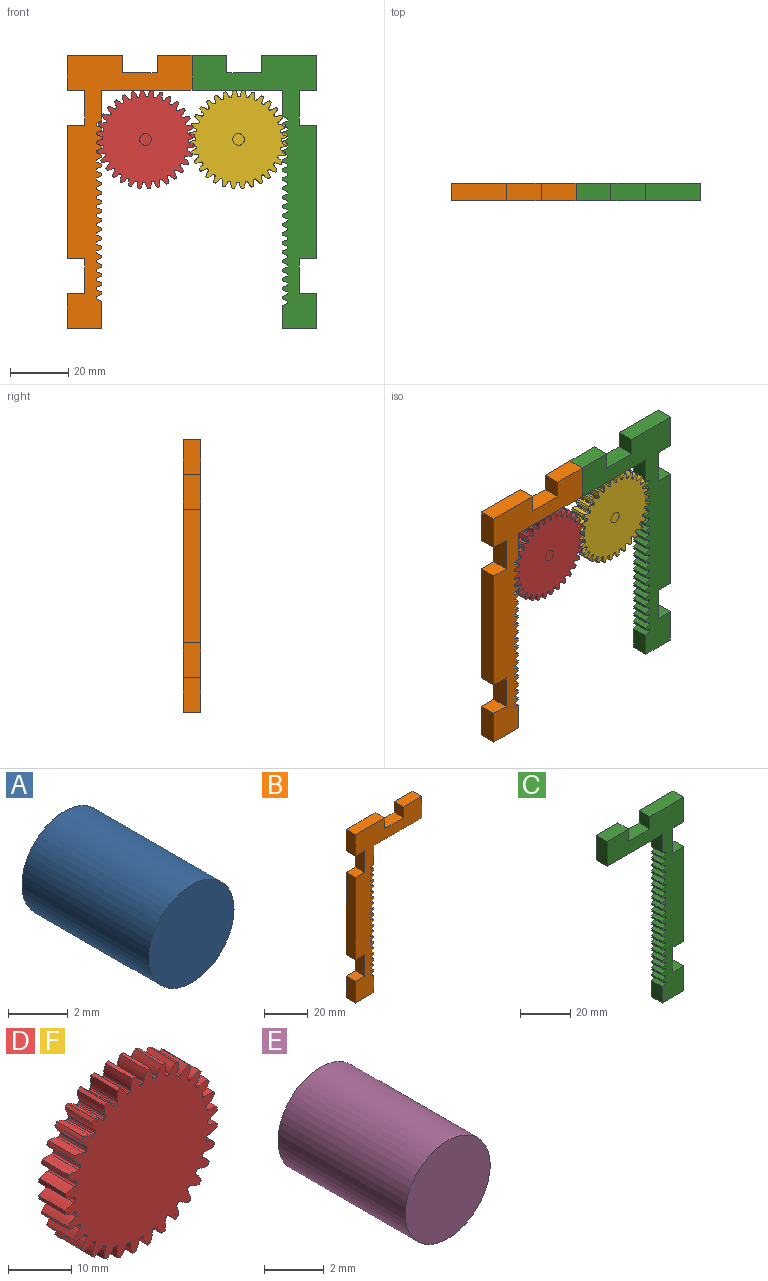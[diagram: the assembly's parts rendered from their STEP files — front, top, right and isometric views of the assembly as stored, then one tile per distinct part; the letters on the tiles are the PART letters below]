
ASSEMBLY  parts=6 mates=5
PART A: 3 faces, bbox 4x6x4 mm
  f0: cylinder r=2mm len=6mm, axis (0,1,0), area 75.4mm2, adj f1,f2
  f1: plane 4x4mm, normal (0,-1,0), area 12.6mm2, adj f0
  f2: plane 4x4mm, normal (0,1,0), area 12.6mm2, adj f0
PART B: 100 faces, bbox 43x6x94 mm
  f0: plane 6x0.84mm, normal (1,0,0), area 5.1mm2, adj f1,f97,f98,f99
  f1: plane 6x2mm, normal (0.34,0,0.94), area 12.8mm2, adj f0,f2,f98,f99
  f2: plane 6x0.84mm, normal (1,0,0), area 5.1mm2, adj f1,f3,f98,f99
  f3: plane 6x2mm, normal (0.34,0,-0.94), area 12.8mm2, adj f2,f4,f98,f99
  f4: plane 10.57x6mm, normal (1,0,0), area 63.4mm2, adj f3,f5,f98,f99
  f5: plane 31x6mm, normal (0,0,-1), area 186mm2, adj f4,f6,f98,f99
  f6: plane 12x6mm, normal (1,0,0), area 72mm2, adj f5,f7,f98,f99
  f7: plane 12x6mm, normal (0,0,1), area 72mm2, adj f6,f8,f98,f99
  f8: plane 6x6mm, normal (-1,0,0), area 36mm2, adj f7,f9,f98,f99
  f9: plane 12x6mm, normal (0,0,1), area 72mm2, adj f8,f10,f98,f99
  f10: plane 6x6mm, normal (1,0,0), area 36mm2, adj f9,f11,f98,f99
  f11: plane 19x6mm, normal (0,0,1), area 114mm2, adj f10,f12,f98,f99
  f12: plane 12x6mm, normal (-1,0,0), area 72mm2, adj f11,f13,f98,f99
  f13: plane 6x6mm, normal (0,0,-1), area 36mm2, adj f12,f14,f98,f99
  f14: plane 12x6mm, normal (-1,0,0), area 72mm2, adj f13,f15,f98,f99
  f15: plane 6x6mm, normal (0,0,1), area 36mm2, adj f14,f16,f98,f99
  f16: plane 46x6mm, normal (-1,0,0), area 276mm2, adj f15,f17,f98,f99
  f17: plane 6x6mm, normal (0,0,-1), area 36mm2, adj f16,f18,f98,f99
  f18: plane 12x6mm, normal (-1,0,0), area 72mm2, adj f17,f19,f98,f99
  f19: plane 6x6mm, normal (0,0,1), area 36mm2, adj f18,f20,f98,f99
  f20: plane 12x6mm, normal (-1,0,0), area 72mm2, adj f19,f21,f98,f99
  f21: plane 12x6mm, normal (0,0,-1), area 72mm2, adj f20,f22,f98,f99
  f22: plane 9.44x6mm, normal (1,0,0), area 56.7mm2, adj f21,f23,f98,f99
  f23: plane 6x2mm, normal (0.34,0,0.94), area 12.8mm2, adj f22,f24,f98,f99
  f24: plane 6x0.84mm, normal (1,0,0), area 5.1mm2, adj f23,f25,f98,f99
  f25: plane 6x2mm, normal (0.34,0,-0.94), area 12.8mm2, adj f24,f26,f98,f99
  f26: plane 6x0.84mm, normal (1,0,0), area 5.1mm2, adj f25,f27,f98,f99
  f27: plane 6x2mm, normal (0.34,0,0.94), area 12.8mm2, adj f26,f28,f98,f99
  f28: plane 6x0.84mm, normal (1,0,0), area 5.1mm2, adj f27,f29,f98,f99
  f29: plane 6x2mm, normal (0.34,0,-0.94), area 12.8mm2, adj f28,f30,f98,f99
  f30: plane 6x0.84mm, normal (1,0,0), area 5.1mm2, adj f29,f31,f98,f99
  f31: plane 6x2mm, normal (0.34,0,0.94), area 12.8mm2, adj f30,f32,f98,f99
  f32: plane 6x0.84mm, normal (1,0,0), area 5.1mm2, adj f31,f33,f98,f99
  f33: plane 6x2mm, normal (0.34,0,-0.94), area 12.8mm2, adj f32,f34,f98,f99
  f34: plane 6x0.84mm, normal (1,0,0), area 5.1mm2, adj f33,f35,f98,f99
  f35: plane 6x2mm, normal (0.34,0,0.94), area 12.8mm2, adj f34,f36,f98,f99
  f36: plane 6x0.84mm, normal (1,0,0), area 5.1mm2, adj f35,f37,f98,f99
  f37: plane 6x2mm, normal (0.34,0,-0.94), area 12.8mm2, adj f36,f38,f98,f99
  f38: plane 6x0.84mm, normal (1,0,0), area 5.1mm2, adj f37,f39,f98,f99
  f39: plane 6x2mm, normal (0.34,0,0.94), area 12.8mm2, adj f38,f40,f98,f99
  f40: plane 6x0.84mm, normal (1,0,0), area 5.1mm2, adj f39,f41,f98,f99
  f41: plane 6x2mm, normal (0.34,0,-0.94), area 12.8mm2, adj f40,f42,f98,f99
  f42: plane 6x0.84mm, normal (1,0,0), area 5.1mm2, adj f41,f43,f98,f99
  f43: plane 6x2mm, normal (0.34,0,0.94), area 12.8mm2, adj f42,f44,f98,f99
  f44: plane 6x0.84mm, normal (1,0,0), area 5.1mm2, adj f43,f45,f98,f99
  f45: plane 6x2mm, normal (0.34,0,-0.94), area 12.8mm2, adj f44,f46,f98,f99
  f46: plane 6x0.84mm, normal (1,0,0), area 5.1mm2, adj f45,f47,f98,f99
  f47: plane 6x2mm, normal (0.34,0,0.94), area 12.8mm2, adj f46,f48,f98,f99
  f48: plane 6x0.84mm, normal (1,0,0), area 5.1mm2, adj f47,f49,f98,f99
  f49: plane 6x2mm, normal (0.34,0,-0.94), area 12.8mm2, adj f48,f50,f98,f99
  f50: plane 6x0.84mm, normal (1,0,0), area 5.1mm2, adj f49,f51,f98,f99
  f51: plane 6x2mm, normal (0.34,0,0.94), area 12.8mm2, adj f50,f52,f98,f99
  f52: plane 6x0.84mm, normal (1,0,0), area 5.1mm2, adj f51,f53,f98,f99
  f53: plane 6x2mm, normal (0.34,0,-0.94), area 12.8mm2, adj f52,f54,f98,f99
  f54: plane 6x0.84mm, normal (1,0,0), area 5.1mm2, adj f53,f55,f98,f99
  f55: plane 6x2mm, normal (0.34,0,0.94), area 12.8mm2, adj f54,f56,f98,f99
  f56: plane 6x0.84mm, normal (1,0,0), area 5.1mm2, adj f55,f57,f98,f99
  f57: plane 6x2mm, normal (0.34,0,-0.94), area 12.8mm2, adj f56,f58,f98,f99
  f58: plane 6x0.84mm, normal (1,0,0), area 5.1mm2, adj f57,f59,f98,f99
  f59: plane 6x2mm, normal (0.34,0,0.94), area 12.8mm2, adj f58,f60,f98,f99
  f60: plane 6x0.84mm, normal (1,0,0), area 5.1mm2, adj f59,f61,f98,f99
  f61: plane 6x2mm, normal (0.34,0,-0.94), area 12.8mm2, adj f60,f62,f98,f99
  f62: plane 6x0.84mm, normal (1,0,0), area 5.1mm2, adj f61,f63,f98,f99
  f63: plane 6x2mm, normal (0.34,0,0.94), area 12.8mm2, adj f62,f64,f98,f99
  f64: plane 6x0.84mm, normal (1,0,0), area 5.1mm2, adj f63,f65,f98,f99
  f65: plane 6x2mm, normal (0.34,0,-0.94), area 12.8mm2, adj f64,f66,f98,f99
  f66: plane 6x0.84mm, normal (1,0,0), area 5.1mm2, adj f65,f67,f98,f99
  f67: plane 6x2mm, normal (0.34,0,0.94), area 12.8mm2, adj f66,f68,f98,f99
  f68: plane 6x0.84mm, normal (1,0,0), area 5.1mm2, adj f67,f69,f98,f99
  f69: plane 6x2mm, normal (0.34,0,-0.94), area 12.8mm2, adj f68,f70,f98,f99
  f70: plane 6x0.84mm, normal (1,0,0), area 5.1mm2, adj f69,f71,f98,f99
  f71: plane 6x2mm, normal (0.34,0,0.94), area 12.8mm2, adj f70,f72,f98,f99
  f72: plane 6x0.84mm, normal (1,0,0), area 5.1mm2, adj f71,f73,f98,f99
  f73: plane 6x2mm, normal (0.34,0,-0.94), area 12.8mm2, adj f72,f74,f98,f99
  f74: plane 6x0.84mm, normal (1,0,0), area 5.1mm2, adj f73,f75,f98,f99
  f75: plane 6x2mm, normal (0.34,0,0.94), area 12.8mm2, adj f74,f76,f98,f99
  f76: plane 6x0.84mm, normal (1,0,0), area 5.1mm2, adj f75,f77,f98,f99
  f77: plane 6x2mm, normal (0.34,0,-0.94), area 12.8mm2, adj f76,f78,f98,f99
  f78: plane 6x0.84mm, normal (1,0,0), area 5.1mm2, adj f77,f79,f98,f99
  f79: plane 6x2mm, normal (0.34,0,0.94), area 12.8mm2, adj f78,f80,f98,f99
  f80: plane 6x0.84mm, normal (1,0,0), area 5.1mm2, adj f79,f81,f98,f99
  f81: plane 6x2mm, normal (0.34,0,-0.94), area 12.8mm2, adj f80,f82,f98,f99
  f82: plane 6x0.84mm, normal (1,0,0), area 5.1mm2, adj f81,f83,f98,f99
  f83: plane 6x2mm, normal (0.34,0,0.94), area 12.8mm2, adj f82,f84,f98,f99
  f84: plane 6x0.84mm, normal (1,0,0), area 5.1mm2, adj f83,f85,f98,f99
  f85: plane 6x2mm, normal (0.34,0,-0.94), area 12.8mm2, adj f84,f86,f98,f99
  f86: plane 6x0.84mm, normal (1,0,0), area 5.1mm2, adj f85,f87,f98,f99
  f87: plane 6x2mm, normal (0.34,0,0.94), area 12.8mm2, adj f86,f88,f98,f99
  f88: plane 6x0.84mm, normal (1,0,0), area 5.1mm2, adj f87,f89,f98,f99
  f89: plane 6x2mm, normal (0.34,0,-0.94), area 12.8mm2, adj f88,f90,f98,f99
  f90: plane 6x0.84mm, normal (1,0,0), area 5.1mm2, adj f89,f91,f98,f99
  f91: plane 6x2mm, normal (0.34,0,0.94), area 12.8mm2, adj f90,f92,f98,f99
  f92: plane 6x0.84mm, normal (1,0,0), area 5.1mm2, adj f91,f93,f98,f99
  f93: plane 6x2mm, normal (0.34,0,-0.94), area 12.8mm2, adj f92,f94,f98,f99
  f94: plane 6x0.84mm, normal (1,0,0), area 5.1mm2, adj f93,f95,f98,f99
  f95: plane 6x2mm, normal (0.34,0,0.94), area 12.8mm2, adj f94,f96,f98,f99
  f96: plane 6x0.84mm, normal (1,0,0), area 5.1mm2, adj f95,f97,f98,f99
  f97: plane 6x2mm, normal (0.34,0,-0.94), area 12.8mm2, adj f0,f96,f98,f99
  f98: plane 94x43mm, normal (0,-1,0), area 1221.2mm2, adj f0,f1,f2,f3,f4,f5,f6,f7
  f99: plane 94x43mm, normal (0,1,0), area 1221.2mm2, adj f0,f1,f2,f3,f4,f5,f6,f7
PART C: 104 faces, bbox 43x6x94 mm
  f0: plane 6x0.84mm, normal (-1,0,0), area 5.1mm2, adj f1,f101,f102,f103
  f1: plane 6x2mm, normal (-0.34,0,0.94), area 12.8mm2, adj f0,f2,f102,f103
  f2: plane 6x0.84mm, normal (-1,0,0), area 5.1mm2, adj f1,f3,f102,f103
  f3: plane 6x2mm, normal (-0.34,0,-0.94), area 12.8mm2, adj f2,f4,f102,f103
  f4: plane 6x0.84mm, normal (-1,0,0), area 5.1mm2, adj f3,f5,f102,f103
  f5: plane 6x2mm, normal (-0.34,0,0.94), area 12.8mm2, adj f4,f6,f102,f103
  f6: plane 6x0.84mm, normal (-1,0,0), area 5.1mm2, adj f5,f7,f102,f103
  f7: plane 6x2mm, normal (-0.34,0,-0.94), area 12.8mm2, adj f6,f8,f102,f103
  f8: plane 6x0.84mm, normal (-1,0,0), area 5.1mm2, adj f7,f9,f102,f103
  f9: plane 6x2mm, normal (-0.34,0,0.94), area 12.8mm2, adj f8,f10,f102,f103
  f10: plane 6x0.84mm, normal (-1,0,0), area 5.1mm2, adj f9,f11,f102,f103
  f11: plane 6x2mm, normal (-0.34,0,-0.94), area 12.8mm2, adj f10,f12,f102,f103
  f12: plane 6x0.84mm, normal (-1,0,0), area 5.1mm2, adj f11,f13,f102,f103
  f13: plane 6x2mm, normal (-0.34,0,0.94), area 12.8mm2, adj f12,f14,f102,f103
  f14: plane 6x0.84mm, normal (-1,0,0), area 5.1mm2, adj f13,f15,f102,f103
  f15: plane 6x2mm, normal (-0.34,0,-0.94), area 12.8mm2, adj f14,f16,f102,f103
  f16: plane 6x0.84mm, normal (-1,0,0), area 5.1mm2, adj f15,f17,f102,f103
  f17: plane 6x2mm, normal (-0.34,0,0.94), area 12.8mm2, adj f16,f18,f102,f103
  f18: plane 6x0.84mm, normal (-1,0,0), area 5.1mm2, adj f17,f19,f102,f103
  f19: plane 6x2mm, normal (-0.34,0,-0.94), area 12.8mm2, adj f18,f20,f102,f103
  f20: plane 6x0.84mm, normal (-1,0,0), area 5.1mm2, adj f19,f21,f102,f103
  f21: plane 6x2mm, normal (-0.34,0,0.94), area 12.8mm2, adj f20,f22,f102,f103
  f22: plane 6x0.84mm, normal (-1,0,0), area 5.1mm2, adj f21,f23,f102,f103
  f23: plane 6x2mm, normal (-0.34,0,-0.94), area 12.8mm2, adj f22,f24,f102,f103
  f24: plane 6x0.84mm, normal (-1,0,0), area 5.1mm2, adj f23,f25,f102,f103
  f25: plane 6x2mm, normal (-0.34,0,0.94), area 12.8mm2, adj f24,f26,f102,f103
  f26: plane 6x0.84mm, normal (-1,0,0), area 5.1mm2, adj f25,f27,f102,f103
  f27: plane 6x2mm, normal (-0.34,0,-0.94), area 12.8mm2, adj f26,f28,f102,f103
  f28: plane 6x0.84mm, normal (-1,0,0), area 5.1mm2, adj f27,f29,f102,f103
  f29: plane 6x2mm, normal (-0.34,0,0.94), area 12.8mm2, adj f28,f30,f102,f103
  f30: plane 6x0.84mm, normal (-1,0,0), area 5.1mm2, adj f29,f31,f102,f103
  f31: plane 6x2mm, normal (-0.34,0,-0.94), area 12.8mm2, adj f30,f32,f102,f103
  f32: plane 6x0.84mm, normal (-1,0,0), area 5.1mm2, adj f31,f33,f102,f103
  f33: plane 6x2mm, normal (-0.34,0,0.94), area 12.8mm2, adj f32,f34,f102,f103
  f34: plane 6x0.84mm, normal (-1,0,0), area 5.1mm2, adj f33,f35,f102,f103
  f35: plane 6x2mm, normal (-0.34,0,-0.94), area 12.8mm2, adj f34,f36,f102,f103
  f36: plane 6x0.84mm, normal (-1,0,0), area 5.1mm2, adj f35,f37,f102,f103
  f37: plane 6x2mm, normal (-0.34,0,0.94), area 12.8mm2, adj f36,f38,f102,f103
  f38: plane 6x0.84mm, normal (-1,0,0), area 5.1mm2, adj f37,f39,f102,f103
  f39: plane 6x2mm, normal (-0.34,0,-0.94), area 12.8mm2, adj f38,f40,f102,f103
  f40: plane 6x0.84mm, normal (-1,0,0), area 5.1mm2, adj f39,f41,f102,f103
  f41: plane 6x2mm, normal (-0.34,0,0.94), area 12.8mm2, adj f40,f42,f102,f103
  f42: plane 6x0.84mm, normal (-1,0,0), area 5.1mm2, adj f41,f43,f102,f103
  f43: plane 6x2mm, normal (-0.34,0,-0.94), area 12.8mm2, adj f42,f44,f102,f103
  f44: plane 6x0.84mm, normal (-1,0,0), area 5.1mm2, adj f43,f45,f102,f103
  f45: plane 6x2mm, normal (-0.34,0,0.94), area 12.8mm2, adj f44,f46,f102,f103
  f46: plane 6x0.84mm, normal (-1,0,0), area 5.1mm2, adj f45,f47,f102,f103
  f47: plane 6x2mm, normal (-0.34,0,-0.94), area 12.8mm2, adj f46,f48,f102,f103
  f48: plane 6x0.84mm, normal (-1,0,0), area 5.1mm2, adj f47,f49,f102,f103
  f49: plane 6x2mm, normal (-0.34,0,0.94), area 12.8mm2, adj f48,f50,f102,f103
  f50: plane 6x0.84mm, normal (-1,0,0), area 5.1mm2, adj f49,f51,f102,f103
  f51: plane 6x2mm, normal (-0.34,0,-0.94), area 12.8mm2, adj f50,f52,f102,f103
  f52: plane 6x0.84mm, normal (-1,0,0), area 5.1mm2, adj f51,f53,f102,f103
  f53: plane 6x2mm, normal (-0.34,0,0.94), area 12.8mm2, adj f52,f54,f102,f103
  f54: plane 6x0.84mm, normal (-1,0,0), area 5.1mm2, adj f53,f55,f102,f103
  f55: plane 6x2mm, normal (-0.34,0,-0.94), area 12.8mm2, adj f54,f56,f102,f103
  f56: plane 6x0.84mm, normal (-1,0,0), area 5.1mm2, adj f55,f57,f102,f103
  f57: plane 6x2mm, normal (-0.34,0,0.94), area 12.8mm2, adj f56,f58,f102,f103
  f58: plane 6x0.84mm, normal (-1,0,0), area 5.1mm2, adj f57,f59,f102,f103
  f59: plane 6x2mm, normal (-0.34,0,-0.94), area 12.8mm2, adj f58,f60,f102,f103
  f60: plane 6x0.84mm, normal (-1,0,0), area 5.1mm2, adj f59,f61,f102,f103
  f61: plane 6x2mm, normal (-0.34,0,0.94), area 12.8mm2, adj f60,f62,f102,f103
  f62: plane 6x0.84mm, normal (-1,0,0), area 5.1mm2, adj f61,f63,f102,f103
  f63: plane 6x2mm, normal (-0.34,0,-0.94), area 12.8mm2, adj f62,f64,f102,f103
  f64: plane 6x0.84mm, normal (-1,0,0), area 5.1mm2, adj f63,f65,f102,f103
  f65: plane 6x2mm, normal (-0.34,0,0.94), area 12.8mm2, adj f64,f66,f102,f103
  f66: plane 6x0.84mm, normal (-1,0,0), area 5.1mm2, adj f65,f67,f102,f103
  f67: plane 6x2mm, normal (-0.34,0,-0.94), area 12.8mm2, adj f66,f68,f102,f103
  f68: plane 6x0.84mm, normal (-1,0,0), area 5.1mm2, adj f67,f69,f102,f103
  f69: plane 6x2mm, normal (-0.34,0,0.94), area 12.8mm2, adj f68,f70,f102,f103
  f70: plane 6x0.84mm, normal (-1,0,0), area 5.1mm2, adj f69,f71,f102,f103
  f71: plane 6x2mm, normal (-0.34,0,-0.94), area 12.8mm2, adj f70,f72,f102,f103
  f72: plane 6x0.84mm, normal (-1,0,0), area 5.1mm2, adj f71,f73,f102,f103
  f73: plane 6x2mm, normal (-0.34,0,0.94), area 12.8mm2, adj f72,f74,f102,f103
  f74: plane 6x0.84mm, normal (-1,0,0), area 5.1mm2, adj f73,f75,f102,f103
  f75: plane 6x2mm, normal (-0.34,0,-0.94), area 12.8mm2, adj f74,f76,f102,f103
  f76: plane 6x0.84mm, normal (-1,0,0), area 5.1mm2, adj f75,f77,f102,f103
  f77: plane 6x2mm, normal (-0.34,0,0.94), area 12.8mm2, adj f76,f78,f102,f103
  f78: plane 7.87x6mm, normal (-1,0,0), area 47.2mm2, adj f77,f79,f102,f103
  f79: plane 12x6mm, normal (0,0,-1), area 72mm2, adj f78,f80,f102,f103
  f80: plane 12x6mm, normal (1,0,0), area 72mm2, adj f79,f81,f102,f103
  f81: plane 6x6mm, normal (0,0,1), area 36mm2, adj f80,f82,f102,f103
  f82: plane 12x6mm, normal (1,0,0), area 72mm2, adj f81,f83,f102,f103
  f83: plane 6x6mm, normal (0,0,-1), area 36mm2, adj f82,f84,f102,f103
  f84: plane 46x6mm, normal (1,0,0), area 276mm2, adj f83,f85,f102,f103
  f85: plane 6x6mm, normal (0,0,1), area 36mm2, adj f84,f86,f102,f103
  f86: plane 12x6mm, normal (1,0,0), area 72mm2, adj f85,f87,f102,f103
  f87: plane 6x6mm, normal (0,0,-1), area 36mm2, adj f86,f88,f102,f103
  f88: plane 12x6mm, normal (1,0,0), area 72mm2, adj f87,f89,f102,f103
  f89: plane 19x6mm, normal (0,0,1), area 114mm2, adj f88,f90,f102,f103
  f90: plane 6x6mm, normal (-1,0,0), area 36mm2, adj f89,f91,f102,f103
  f91: plane 12x6mm, normal (0,0,1), area 72mm2, adj f90,f92,f102,f103
  f92: plane 6x6mm, normal (1,0,0), area 36mm2, adj f91,f93,f102,f103
  f93: plane 12x6mm, normal (0,0,1), area 72mm2, adj f92,f94,f102,f103
  f94: plane 12x6mm, normal (-1,0,0), area 72mm2, adj f93,f95,f102,f103
  f95: plane 31x6mm, normal (0,0,-1), area 186mm2, adj f94,f96,f102,f103
  f96: plane 9x6mm, normal (-1,0,0), area 54mm2, adj f95,f97,f102,f103
  f97: plane 6x2mm, normal (-0.34,0,-0.94), area 12.8mm2, adj f96,f98,f102,f103
  f98: plane 6x0.84mm, normal (-1,0,0), area 5.1mm2, adj f97,f99,f102,f103
  f99: plane 6x2mm, normal (-0.34,0,0.94), area 12.8mm2, adj f98,f100,f102,f103
  f100: plane 6x0.84mm, normal (-1,0,0), area 5.1mm2, adj f99,f101,f102,f103
  f101: plane 6x2mm, normal (-0.34,0,-0.94), area 12.8mm2, adj f0,f100,f102,f103
  f102: plane 94x43mm, normal (0,-1,0), area 1218mm2, adj f0,f1,f2,f3,f4,f5,f6,f7
  f103: plane 94x43mm, normal (0,1,0), area 1218mm2, adj f0,f1,f2,f3,f4,f5,f6,f7
PART D: 194 faces, bbox 33.9x6x33.9 mm
  f0: cylinder r=17mm len=6mm, axis (0,1,0), area 4.4mm2, adj f31,f33,f119,f191
  f1: cylinder r=17mm len=6mm, axis (0,1,0), area 4.4mm2, adj f31,f33,f186,f189
  f2: cylinder r=17mm len=6mm, axis (0,1,0), area 4.4mm2, adj f31,f33,f174,f181
  f3: cylinder r=17mm len=6mm, axis (0,1,0), area 4.4mm2, adj f31,f33,f176,f184
  f4: cylinder r=17mm len=6mm, axis (0,1,0), area 4.4mm2, adj f31,f33,f171,f179
  f5: cylinder r=17mm len=6mm, axis (0,1,0), area 4.4mm2, adj f31,f33,f166,f169
  f6: cylinder r=17mm len=6mm, axis (0,1,0), area 4.4mm2, adj f31,f33,f161,f164
  f7: cylinder r=17mm len=6mm, axis (0,1,0), area 4.4mm2, adj f31,f33,f79,f156
  f8: cylinder r=17mm len=6mm, axis (0,1,0), area 4.4mm2, adj f31,f33,f151,f154
  f9: cylinder r=17mm len=6mm, axis (0,1,0), area 4.4mm2, adj f31,f33,f139,f146
  f10: cylinder r=17mm len=6mm, axis (0,1,0), area 4.4mm2, adj f31,f33,f141,f149
  f11: cylinder r=17mm len=6mm, axis (0,1,0), area 4.4mm2, adj f31,f33,f136,f144
  f12: cylinder r=17mm len=6mm, axis (0,1,0), area 4.4mm2, adj f31,f33,f131,f134
  f13: cylinder r=17mm len=6mm, axis (0,1,0), area 4.4mm2, adj f31,f33,f126,f129
  f14: cylinder r=17mm len=6mm, axis (0,1,0), area 4.4mm2, adj f31,f33,f121,f124
  f15: cylinder r=17mm len=6mm, axis (0,1,0), area 4.4mm2, adj f31,f33,f39,f116
  f16: cylinder r=17mm len=6mm, axis (0,1,0), area 4.4mm2, adj f31,f33,f111,f114
  f17: cylinder r=17mm len=6mm, axis (0,1,0), area 4.4mm2, adj f31,f33,f99,f106
  f18: cylinder r=17mm len=6mm, axis (0,1,0), area 4.4mm2, adj f31,f33,f101,f109
  f19: cylinder r=17mm len=6mm, axis (0,1,0), area 4.4mm2, adj f31,f33,f96,f104
  f20: cylinder r=17mm len=6mm, axis (0,1,0), area 4.4mm2, adj f31,f33,f91,f94
  f21: cylinder r=17mm len=6mm, axis (0,1,0), area 4.4mm2, adj f31,f33,f86,f89
  f22: cylinder r=17mm len=6mm, axis (0,1,0), area 4.4mm2, adj f31,f33,f81,f84
  f23: cylinder r=17mm len=6mm, axis (0,1,0), area 4.4mm2, adj f31,f33,f34,f76
  f24: cylinder r=17mm len=6mm, axis (0,1,0), area 4.4mm2, adj f31,f33,f71,f74
  f25: cylinder r=17mm len=6mm, axis (0,1,0), area 4.4mm2, adj f31,f33,f59,f66
  f26: cylinder r=17mm len=6mm, axis (0,1,0), area 4.4mm2, adj f31,f33,f61,f69
  f27: cylinder r=17mm len=6mm, axis (0,1,0), area 4.4mm2, adj f31,f33,f56,f64
  f28: cylinder r=17mm len=6mm, axis (0,1,0), area 4.4mm2, adj f31,f33,f51,f54
  f29: cylinder r=17mm len=6mm, axis (0,1,0), area 4.4mm2, adj f31,f33,f46,f49
  f30: cylinder r=17mm len=6mm, axis (0,1,0), area 4.4mm2, adj f31,f33,f41,f44
  f31: plane 33.9x33.9mm, normal (0,-1,0), area 796.1mm2, adj f0,f1,f2,f3,f4,f5,f6,f7
  f32: cylinder r=17mm len=6mm, axis (0,1,0), area 4.4mm2, adj f31,f33,f36,f159
  f33: plane 33.9x33.9mm, normal (0,1,0), area 796.1mm2, adj f0,f1,f2,f3,f4,f5,f6,f7
  f34: extruded ~6x1.88mm, area 12.3mm2, adj f23,f31,f33,f37
  f35: cylinder r=14.75mm len=6mm, axis (0,1,0), area 1.8mm2, adj f31,f33,f37,f38
  f36: extruded ~6x1.88mm, area 12.3mm2, adj f31,f32,f33,f38
  f37: cylinder r=0.36mm len=6mm, axis (0,1,0), area 3.2mm2, adj f31,f33,f34,f35
  f38: cylinder r=0.36mm len=6mm, axis (0,1,0), area 3.2mm2, adj f31,f33,f35,f36
  f39: extruded ~6x1.88mm, area 12.3mm2, adj f15,f31,f33,f42
  f40: cylinder r=14.75mm len=6mm, axis (0,1,0), area 1.8mm2, adj f31,f33,f42,f43
  f41: extruded ~6x1.88mm, area 12.3mm2, adj f30,f31,f33,f43
  f42: cylinder r=0.36mm len=6mm, axis (0,1,0), area 3.2mm2, adj f31,f33,f39,f40
  f43: cylinder r=0.36mm len=6mm, axis (0,1,0), area 3.2mm2, adj f31,f33,f40,f41
  f44: extruded ~6x1.99mm, area 12.3mm2, adj f30,f31,f33,f47
  f45: cylinder r=14.75mm len=6mm, axis (0,1,0), area 1.8mm2, adj f31,f33,f47,f48
  f46: extruded ~6x1.69mm, area 12.3mm2, adj f29,f31,f33,f48
  f47: cylinder r=0.36mm len=6mm, axis (0,1,0), area 3.2mm2, adj f31,f33,f44,f45
  f48: cylinder r=0.36mm len=6mm, axis (0,1,0), area 3.2mm2, adj f31,f33,f45,f46
  f49: extruded ~6x2.03mm, area 12.3mm2, adj f29,f31,f33,f52
  f50: cylinder r=14.75mm len=6mm, axis (0,1,0), area 1.8mm2, adj f31,f33,f52,f53
  f51: extruded ~6x1.44mm, area 12.3mm2, adj f28,f31,f33,f53
  f52: cylinder r=0.36mm len=6mm, axis (0,1,0), area 3.2mm2, adj f31,f33,f49,f50
  f53: cylinder r=0.36mm len=6mm, axis (0,1,0), area 3.2mm2, adj f31,f33,f50,f51
  f54: extruded ~6x1.99mm, area 12.3mm2, adj f28,f31,f33,f57
  f55: cylinder r=14.75mm len=6mm, axis (0,1,0), area 1.8mm2, adj f31,f33,f57,f58
  f56: extruded ~6x1.69mm, area 12.3mm2, adj f27,f31,f33,f58
  f57: cylinder r=0.36mm len=6mm, axis (0,1,0), area 3.2mm2, adj f31,f33,f54,f55
  f58: cylinder r=0.36mm len=6mm, axis (0,1,0), area 3.2mm2, adj f31,f33,f55,f56
  f59: extruded ~6x1.69mm, area 12.3mm2, adj f25,f31,f33,f62
  f60: cylinder r=14.75mm len=6mm, axis (0,1,0), area 1.8mm2, adj f31,f33,f62,f63
  f61: extruded ~6x1.99mm, area 12.3mm2, adj f26,f31,f33,f63
  f62: cylinder r=0.36mm len=6mm, axis (0,1,0), area 3.2mm2, adj f31,f33,f59,f60
  f63: cylinder r=0.36mm len=6mm, axis (0,1,0), area 3.2mm2, adj f31,f33,f60,f61
  f64: extruded ~6x1.88mm, area 12.3mm2, adj f27,f31,f33,f67
  f65: cylinder r=14.75mm len=6mm, axis (0,1,0), area 1.8mm2, adj f31,f33,f67,f68
  f66: extruded ~6x1.88mm, area 12.3mm2, adj f25,f31,f33,f68
  f67: cylinder r=0.36mm len=6mm, axis (0,1,0), area 3.2mm2, adj f31,f33,f64,f65
  f68: cylinder r=0.36mm len=6mm, axis (0,1,0), area 3.2mm2, adj f31,f33,f65,f66
  f69: extruded ~6x1.44mm, area 12.3mm2, adj f26,f31,f33,f72
  f70: cylinder r=14.75mm len=6mm, axis (0,1,0), area 1.8mm2, adj f31,f33,f72,f73
  f71: extruded ~6x2.03mm, area 12.3mm2, adj f24,f31,f33,f73
  f72: cylinder r=0.36mm len=6mm, axis (0,1,0), area 3.2mm2, adj f31,f33,f69,f70
  f73: cylinder r=0.36mm len=6mm, axis (0,1,0), area 3.2mm2, adj f31,f33,f70,f71
  f74: extruded ~6x1.69mm, area 12.3mm2, adj f24,f31,f33,f77
  f75: cylinder r=14.75mm len=6mm, axis (0,1,0), area 1.8mm2, adj f31,f33,f77,f78
  f76: extruded ~6x1.99mm, area 12.3mm2, adj f23,f31,f33,f78
  f77: cylinder r=0.36mm len=6mm, axis (0,1,0), area 3.2mm2, adj f31,f33,f74,f75
  f78: cylinder r=0.36mm len=6mm, axis (0,1,0), area 3.2mm2, adj f31,f33,f75,f76
  f79: extruded ~6x1.88mm, area 12.3mm2, adj f7,f31,f33,f82
  f80: cylinder r=14.75mm len=6mm, axis (0,1,0), area 1.8mm2, adj f31,f33,f82,f83
  f81: extruded ~6x1.88mm, area 12.3mm2, adj f22,f31,f33,f83
  f82: cylinder r=0.36mm len=6mm, axis (0,1,0), area 3.2mm2, adj f31,f33,f79,f80
  f83: cylinder r=0.36mm len=6mm, axis (0,1,0), area 3.2mm2, adj f31,f33,f80,f81
  f84: extruded ~6x1.99mm, area 12.3mm2, adj f22,f31,f33,f87
  f85: cylinder r=14.75mm len=6mm, axis (0,1,0), area 1.8mm2, adj f31,f33,f87,f88
  f86: extruded ~6x1.69mm, area 12.3mm2, adj f21,f31,f33,f88
  f87: cylinder r=0.36mm len=6mm, axis (0,1,0), area 3.2mm2, adj f31,f33,f84,f85
  f88: cylinder r=0.36mm len=6mm, axis (0,1,0), area 3.2mm2, adj f31,f33,f85,f86
  f89: extruded ~6x2.03mm, area 12.3mm2, adj f21,f31,f33,f92
  f90: cylinder r=14.75mm len=6mm, axis (0,1,0), area 1.8mm2, adj f31,f33,f92,f93
  f91: extruded ~6x1.44mm, area 12.3mm2, adj f20,f31,f33,f93
  f92: cylinder r=0.36mm len=6mm, axis (0,1,0), area 3.2mm2, adj f31,f33,f89,f90
  f93: cylinder r=0.36mm len=6mm, axis (0,1,0), area 3.2mm2, adj f31,f33,f90,f91
  f94: extruded ~6x1.99mm, area 12.3mm2, adj f20,f31,f33,f97
  f95: cylinder r=14.75mm len=6mm, axis (0,1,0), area 1.8mm2, adj f31,f33,f97,f98
  f96: extruded ~6x1.69mm, area 12.3mm2, adj f19,f31,f33,f98
  f97: cylinder r=0.36mm len=6mm, axis (0,1,0), area 3.2mm2, adj f31,f33,f94,f95
  f98: cylinder r=0.36mm len=6mm, axis (0,1,0), area 3.2mm2, adj f31,f33,f95,f96
  f99: extruded ~6x1.69mm, area 12.3mm2, adj f17,f31,f33,f102
  f100: cylinder r=14.75mm len=6mm, axis (0,1,0), area 1.8mm2, adj f31,f33,f102,f103
  f101: extruded ~6x1.99mm, area 12.3mm2, adj f18,f31,f33,f103
  f102: cylinder r=0.36mm len=6mm, axis (0,1,0), area 3.2mm2, adj f31,f33,f99,f100
  f103: cylinder r=0.36mm len=6mm, axis (0,1,0), area 3.2mm2, adj f31,f33,f100,f101
  f104: extruded ~6x1.88mm, area 12.3mm2, adj f19,f31,f33,f107
  f105: cylinder r=14.75mm len=6mm, axis (0,1,0), area 1.8mm2, adj f31,f33,f107,f108
  f106: extruded ~6x1.88mm, area 12.3mm2, adj f17,f31,f33,f108
  f107: cylinder r=0.36mm len=6mm, axis (0,1,0), area 3.2mm2, adj f31,f33,f104,f105
  f108: cylinder r=0.36mm len=6mm, axis (0,1,0), area 3.2mm2, adj f31,f33,f105,f106
  f109: extruded ~6x1.44mm, area 12.3mm2, adj f18,f31,f33,f112
  f110: cylinder r=14.75mm len=6mm, axis (0,1,0), area 1.8mm2, adj f31,f33,f112,f113
  f111: extruded ~6x2.03mm, area 12.3mm2, adj f16,f31,f33,f113
  f112: cylinder r=0.36mm len=6mm, axis (0,1,0), area 3.2mm2, adj f31,f33,f109,f110
  f113: cylinder r=0.36mm len=6mm, axis (0,1,0), area 3.2mm2, adj f31,f33,f110,f111
  f114: extruded ~6x1.69mm, area 12.3mm2, adj f16,f31,f33,f117
  f115: cylinder r=14.75mm len=6mm, axis (0,1,0), area 1.8mm2, adj f31,f33,f117,f118
  f116: extruded ~6x1.99mm, area 12.3mm2, adj f15,f31,f33,f118
  f117: cylinder r=0.36mm len=6mm, axis (0,1,0), area 3.2mm2, adj f31,f33,f114,f115
  f118: cylinder r=0.36mm len=6mm, axis (0,1,0), area 3.2mm2, adj f31,f33,f115,f116
  f119: extruded ~6x1.88mm, area 12.3mm2, adj f0,f31,f33,f122
  f120: cylinder r=14.75mm len=6mm, axis (0,1,0), area 1.8mm2, adj f31,f33,f122,f123
  f121: extruded ~6x1.88mm, area 12.3mm2, adj f14,f31,f33,f123
  f122: cylinder r=0.36mm len=6mm, axis (0,1,0), area 3.2mm2, adj f31,f33,f119,f120
  f123: cylinder r=0.36mm len=6mm, axis (0,1,0), area 3.2mm2, adj f31,f33,f120,f121
  f124: extruded ~6x1.99mm, area 12.3mm2, adj f14,f31,f33,f127
  f125: cylinder r=14.75mm len=6mm, axis (0,1,0), area 1.8mm2, adj f31,f33,f127,f128
  f126: extruded ~6x1.69mm, area 12.3mm2, adj f13,f31,f33,f128
  f127: cylinder r=0.36mm len=6mm, axis (0,1,0), area 3.2mm2, adj f31,f33,f124,f125
  f128: cylinder r=0.36mm len=6mm, axis (0,1,0), area 3.2mm2, adj f31,f33,f125,f126
  f129: extruded ~6x2.03mm, area 12.3mm2, adj f13,f31,f33,f132
  f130: cylinder r=14.75mm len=6mm, axis (0,1,0), area 1.8mm2, adj f31,f33,f132,f133
  f131: extruded ~6x1.44mm, area 12.3mm2, adj f12,f31,f33,f133
  f132: cylinder r=0.36mm len=6mm, axis (0,1,0), area 3.2mm2, adj f31,f33,f129,f130
  f133: cylinder r=0.36mm len=6mm, axis (0,1,0), area 3.2mm2, adj f31,f33,f130,f131
  f134: extruded ~6x1.99mm, area 12.3mm2, adj f12,f31,f33,f137
  f135: cylinder r=14.75mm len=6mm, axis (0,1,0), area 1.8mm2, adj f31,f33,f137,f138
  f136: extruded ~6x1.69mm, area 12.3mm2, adj f11,f31,f33,f138
  f137: cylinder r=0.36mm len=6mm, axis (0,1,0), area 3.2mm2, adj f31,f33,f134,f135
  f138: cylinder r=0.36mm len=6mm, axis (0,1,0), area 3.2mm2, adj f31,f33,f135,f136
  f139: extruded ~6x1.69mm, area 12.3mm2, adj f9,f31,f33,f142
  f140: cylinder r=14.75mm len=6mm, axis (0,1,0), area 1.8mm2, adj f31,f33,f142,f143
  f141: extruded ~6x1.99mm, area 12.3mm2, adj f10,f31,f33,f143
  f142: cylinder r=0.36mm len=6mm, axis (0,1,0), area 3.2mm2, adj f31,f33,f139,f140
  f143: cylinder r=0.36mm len=6mm, axis (0,1,0), area 3.2mm2, adj f31,f33,f140,f141
  f144: extruded ~6x1.88mm, area 12.3mm2, adj f11,f31,f33,f147
  f145: cylinder r=14.75mm len=6mm, axis (0,1,0), area 1.8mm2, adj f31,f33,f147,f148
  f146: extruded ~6x1.88mm, area 12.3mm2, adj f9,f31,f33,f148
  f147: cylinder r=0.36mm len=6mm, axis (0,1,0), area 3.2mm2, adj f31,f33,f144,f145
  f148: cylinder r=0.36mm len=6mm, axis (0,1,0), area 3.2mm2, adj f31,f33,f145,f146
  f149: extruded ~6x1.44mm, area 12.3mm2, adj f10,f31,f33,f152
  f150: cylinder r=14.75mm len=6mm, axis (0,1,0), area 1.8mm2, adj f31,f33,f152,f153
  f151: extruded ~6x2.03mm, area 12.3mm2, adj f8,f31,f33,f153
  f152: cylinder r=0.36mm len=6mm, axis (0,1,0), area 3.2mm2, adj f31,f33,f149,f150
  f153: cylinder r=0.36mm len=6mm, axis (0,1,0), area 3.2mm2, adj f31,f33,f150,f151
  f154: extruded ~6x1.69mm, area 12.3mm2, adj f8,f31,f33,f157
  f155: cylinder r=14.75mm len=6mm, axis (0,1,0), area 1.8mm2, adj f31,f33,f157,f158
  f156: extruded ~6x1.99mm, area 12.3mm2, adj f7,f31,f33,f158
  f157: cylinder r=0.36mm len=6mm, axis (0,1,0), area 3.2mm2, adj f31,f33,f154,f155
  f158: cylinder r=0.36mm len=6mm, axis (0,1,0), area 3.2mm2, adj f31,f33,f155,f156
  f159: extruded ~6x1.99mm, area 12.3mm2, adj f31,f32,f33,f162
  f160: cylinder r=14.75mm len=6mm, axis (0,1,0), area 1.8mm2, adj f31,f33,f162,f163
  f161: extruded ~6x1.69mm, area 12.3mm2, adj f6,f31,f33,f163
  f162: cylinder r=0.36mm len=6mm, axis (0,1,0), area 3.2mm2, adj f31,f33,f159,f160
  f163: cylinder r=0.36mm len=6mm, axis (0,1,0), area 3.2mm2, adj f31,f33,f160,f161
  f164: extruded ~6x2.03mm, area 12.3mm2, adj f6,f31,f33,f167
  f165: cylinder r=14.75mm len=6mm, axis (0,1,0), area 1.8mm2, adj f31,f33,f167,f168
  f166: extruded ~6x1.44mm, area 12.3mm2, adj f5,f31,f33,f168
  f167: cylinder r=0.36mm len=6mm, axis (0,1,0), area 3.2mm2, adj f31,f33,f164,f165
  f168: cylinder r=0.36mm len=6mm, axis (0,1,0), area 3.2mm2, adj f31,f33,f165,f166
  f169: extruded ~6x1.99mm, area 12.3mm2, adj f5,f31,f33,f172
  f170: cylinder r=14.75mm len=6mm, axis (0,1,0), area 1.8mm2, adj f31,f33,f172,f173
  f171: extruded ~6x1.69mm, area 12.3mm2, adj f4,f31,f33,f173
  f172: cylinder r=0.36mm len=6mm, axis (0,1,0), area 3.2mm2, adj f31,f33,f169,f170
  f173: cylinder r=0.36mm len=6mm, axis (0,1,0), area 3.2mm2, adj f31,f33,f170,f171
  f174: extruded ~6x1.69mm, area 12.3mm2, adj f2,f31,f33,f177
  f175: cylinder r=14.75mm len=6mm, axis (0,1,0), area 1.8mm2, adj f31,f33,f177,f178
  f176: extruded ~6x1.99mm, area 12.3mm2, adj f3,f31,f33,f178
  f177: cylinder r=0.36mm len=6mm, axis (0,1,0), area 3.2mm2, adj f31,f33,f174,f175
  f178: cylinder r=0.36mm len=6mm, axis (0,1,0), area 3.2mm2, adj f31,f33,f175,f176
  f179: extruded ~6x1.88mm, area 12.3mm2, adj f4,f31,f33,f182
  f180: cylinder r=14.75mm len=6mm, axis (0,1,0), area 1.8mm2, adj f31,f33,f182,f183
  f181: extruded ~6x1.88mm, area 12.3mm2, adj f2,f31,f33,f183
  f182: cylinder r=0.36mm len=6mm, axis (0,1,0), area 3.2mm2, adj f31,f33,f179,f180
  f183: cylinder r=0.36mm len=6mm, axis (0,1,0), area 3.2mm2, adj f31,f33,f180,f181
  f184: extruded ~6x1.44mm, area 12.3mm2, adj f3,f31,f33,f187
  f185: cylinder r=14.75mm len=6mm, axis (0,1,0), area 1.8mm2, adj f31,f33,f187,f188
  f186: extruded ~6x2.03mm, area 12.3mm2, adj f1,f31,f33,f188
  f187: cylinder r=0.36mm len=6mm, axis (0,1,0), area 3.2mm2, adj f31,f33,f184,f185
  f188: cylinder r=0.36mm len=6mm, axis (0,1,0), area 3.2mm2, adj f31,f33,f185,f186
  f189: extruded ~6x1.69mm, area 12.3mm2, adj f1,f31,f33,f192
  f190: cylinder r=14.75mm len=6mm, axis (0,1,0), area 1.8mm2, adj f31,f33,f192,f193
  f191: extruded ~6x1.99mm, area 12.3mm2, adj f0,f31,f33,f193
  f192: cylinder r=0.36mm len=6mm, axis (0,1,0), area 3.2mm2, adj f31,f33,f189,f190
  f193: cylinder r=0.36mm len=6mm, axis (0,1,0), area 3.2mm2, adj f31,f33,f190,f191
PART E: 3 faces, bbox 4x6x4 mm
  f0: cylinder r=2mm len=6mm, axis (0,1,0), area 75.4mm2, adj f1,f2
  f1: plane 4x4mm, normal (0,-1,0), area 12.6mm2, adj f0
  f2: plane 4x4mm, normal (0,1,0), area 12.6mm2, adj f0
PART F: same geometry as D
PLACE A t=(-13,3,-23.94)mm fixed
PLACE B t=(-13,3,-25.03)mm
PLACE C t=(-73,3,-25.03)mm
PLACE D rot(axis=(0,-1,0),88.3deg) t=(2,3,-41.94)mm
PLACE E t=(-73,3,-23.94)mm fixed
PLACE F rot(axis=(0,-1,0),111.9deg) t=(34,3,-41.94)mm
MATE planar B.f6 <-> C.f94  axis (1,0,0) through (18,0,-19.03)mm
MATE revolute D.f0 <-> A.f0  axis (0,-1,0) through (2,-3,-41.94)mm
MATE planar B.f7 <-> C.f93  axis (0,0,1) through (18,-3,-13.03)mm
MATE planar B.f98 <-> C.f102  axis (0,-1,0) through (-13.48,-3,-49.8)mm
MATE revolute F.f0 <-> E.f0  axis (0,-1,0) through (34,-3,-41.94)mm
